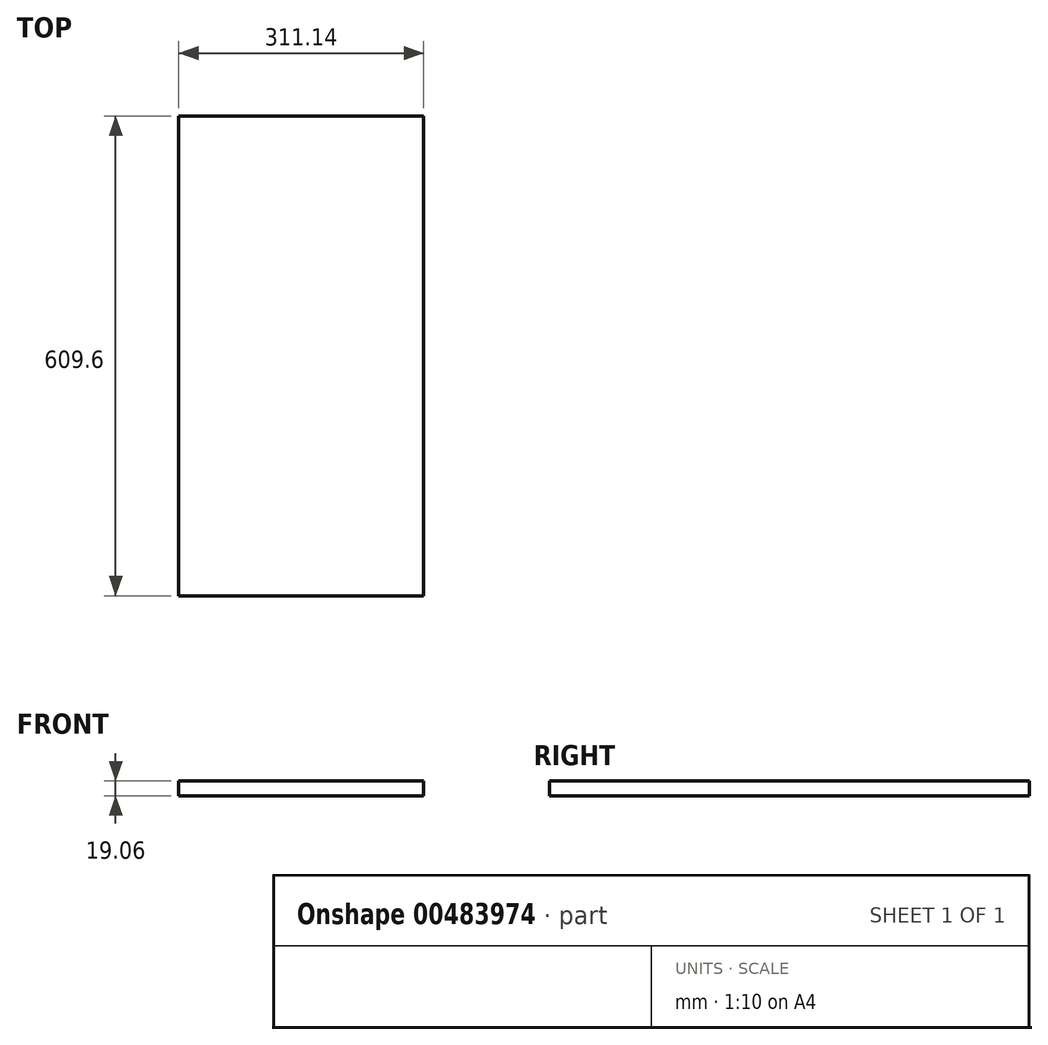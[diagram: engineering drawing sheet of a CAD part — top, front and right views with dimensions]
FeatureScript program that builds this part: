
annotation { "Feature Type Name" : "Feature", "Feature Type Description" : "" }
export const myFeature = defineFeature(function(context is Context, id is Id, definition is map)
    precondition{}
    {
        {
            var Q0;
            Q0=qCreatedBy(makeId("Front.planeOp"),FACE);
            var sketch = newSketch(context, id + "F0", { "sketchPlane" : qUnion([Q0])});
            skLineSegment(sketch, "E0.bottom", {"start": v(155.58, 9.53) * mm, "end": v(-155.58, 9.53) * mm});
            skLineSegment(sketch, "E0.top", {"start": v(155.58, -9.53) * mm, "end": v(-155.58, -9.53) * mm});
            skLineSegment(sketch, "E0.left", {"start": v(155.58, 9.53) * mm, "end": v(155.58, -9.53) * mm});
            skLineSegment(sketch, "E0.right", {"start": v(-155.58, 9.53) * mm, "end": v(-155.58, -9.53) * mm});
            skPoint(sketch, "E0.middle", {"position": v(0, 0) * mm});
            skSolve(sketch);
        }
        {
            var Q0;
            Q0 = qSketchRegion(id + "F0", true);
            extrude(context, id + "F1", {"entities" : qUnion([Q0]), "depth" : 609.6 * mm});
        }
    });
